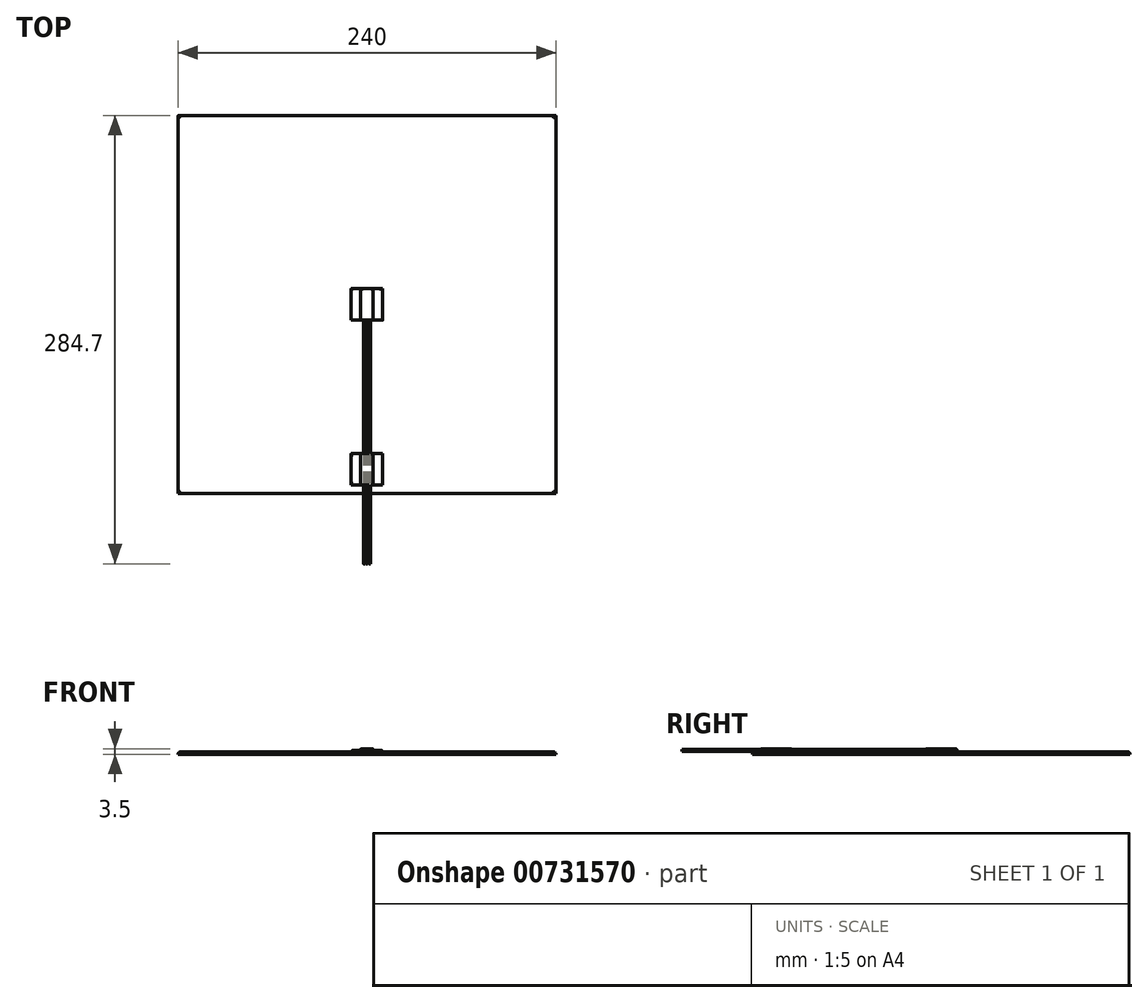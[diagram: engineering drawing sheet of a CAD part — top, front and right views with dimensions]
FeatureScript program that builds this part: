
annotation { "Feature Type Name" : "Feature", "Feature Type Description" : "" }
export const myFeature = defineFeature(function(context is Context, id is Id, definition is map)
    precondition{}
    {
        {
            var Q0;
            Q0=qCreatedBy(makeId("Top.planeOp"),FACE);
            var sketch = newSketch(context, id + "F0", { "sketchPlane" : qUnion([Q0])});
            skCircle(sketch, "E0.cCircle", {"center": v(0, 0) * mm, "radius": 120 * mm, "construction": true});
            skLineSegment(sketch, "E0.0", {"start": v(-120, 120) * mm, "end": v(120, 120) * mm});
            skLineSegment(sketch, "E0.1", {"start": v(120, 120) * mm, "end": v(120, -120) * mm});
            skLineSegment(sketch, "E0.2", {"start": v(120, -120) * mm, "end": v(-120, -120) * mm});
            skLineSegment(sketch, "E0.3", {"start": v(-120, -120) * mm, "end": v(-120, 120) * mm});
            skPoint(sketch, "E0.0.midPoint", {"position": v(0, 120) * mm});
            skSolve(sketch);
        }
        {
            var Q0;
            Q0 = qSketchRegion(id + "F0", true);
            extrude(context, id + "F1", {"entities" : qUnion([Q0]), "depth" : 1.5 * mm, "offsetDistance" : 25 * mm});
        }
        {
            var Q0;
            Q0=makeQuery(id+"F1.opExtrude","CAP_FACE",FACE,{"disambiguationData":[OSD([sQuery(id+"F0.wireOp",EDGE,"E0.0"),sQuery(id+"F0.wireOp",EDGE,"E0.1"),sQuery(id+"F0.wireOp",EDGE,"E0.2"),sQuery(id+"F0.wireOp",EDGE,"E0.3")])],"isStart":false});
            fillet(context, id + "F2", {"entities" : qUnion([Q0]), "radius" : 1.5 * mm, "tangentPropagation" : true, "allowEdgeOverflow" : false});
        }
        {
            var Q0;
            Q0=makeQuery(id+"F1.opExtrude","CAP_FACE",FACE,{"disambiguationData":[OSD([sQuery(id+"F0.wireOp",EDGE,"E0.0"),sQuery(id+"F0.wireOp",EDGE,"E0.1"),sQuery(id+"F0.wireOp",EDGE,"E0.2"),sQuery(id+"F0.wireOp",EDGE,"E0.3")])],"isStart":false});
            var sketch = newSketch(context, id + "F3", { "sketchPlane" : qUnion([Q0])});
            skCircle(sketch, "E1.cCircle", {"center": v(0, 0) * mm, "radius": 10 * mm, "construction": true});
            skLineSegment(sketch, "E1.0", {"start": v(-10, 10) * mm, "end": v(10, 10) * mm});
            skLineSegment(sketch, "E1.1", {"start": v(10, 10) * mm, "end": v(10, -10) * mm});
            skLineSegment(sketch, "E1.2", {"start": v(10, -10) * mm, "end": v(-10, -10) * mm});
            skLineSegment(sketch, "E1.3", {"start": v(-10, -10) * mm, "end": v(-10, 10) * mm});
            skPoint(sketch, "E1.0.midPoint", {"position": v(0, 10) * mm});
            skLineSegment(sketch, "E2", {"start": v(0, 0) * mm, "end": v(0, -105) * mm, "construction": true});
            skCircle(sketch, "E3.cCircle", {"center": v(0, -105) * mm, "radius": 10 * mm, "construction": true});
            skLineSegment(sketch, "E3.0", {"start": v(-10, -95) * mm, "end": v(10, -95) * mm});
            skLineSegment(sketch, "E3.1", {"start": v(10, -95) * mm, "end": v(10, -115) * mm});
            skLineSegment(sketch, "E3.2", {"start": v(10, -115) * mm, "end": v(-10, -115) * mm});
            skLineSegment(sketch, "E3.3", {"start": v(-10, -115) * mm, "end": v(-10, -95) * mm});
            skPoint(sketch, "E3.0.midPoint", {"position": v(0, -95) * mm});
            skSolve(sketch);
        }
        {
            var Q0;
            Q0=qCreatedBy(makeId("Front.planeOp"),FACE);
            var sketch = newSketch(context, id + "F4", { "sketchPlane" : qUnion([Q0])});
            skLineSegment(sketch, "E4", {"start": v(-10, 1.5) * mm, "end": v(-10, 2.5) * mm});
            skLineSegment(sketch, "E5", {"start": v(-10, 2.5) * mm, "end": v(-4, 2.5) * mm});
            skLineSegment(sketch, "E6", {"start": v(4, 2.5) * mm, "end": v(10, 2.5) * mm});
            skLineSegment(sketch, "E7", {"start": v(10, 2.5) * mm, "end": v(10, 1.5) * mm});
            skLineSegment(sketch, "E8", {"start": v(10, 1.5) * mm, "end": v(-10, 1.5) * mm});
            skLineSegment(sketch, "E9", {"start": v(-4, 2.5) * mm, "end": v(-4, 3.5) * mm});
            skLineSegment(sketch, "E10", {"start": v(-4, 3.5) * mm, "end": v(4, 3.5) * mm});
            skLineSegment(sketch, "E11", {"start": v(4, 3.5) * mm, "end": v(4, 2.5) * mm});
            skPoint(sketch, "E12.orphan", {"position": v(0, 2.5) * mm});
            skSolve(sketch);
        }
        {
            var Q0;
            Q0 = qSketchRegion(id + "F4", true);
            extrude(context, id + "F5", {"entities" : qUnion([Q0]), "depth" : 20 * mm, "offsetDistance" : 25 * mm, "symmetric" : true});
        }
        {
            var Q0;
            Q0=makeQuery(id+"F5.opExtrude","SWEPT_EDGE",EDGE,{"disambiguationData":[OSD([sQuery(id+"F4.wireOp",EDGE,"E10"),sQuery(id+"F4.wireOp",EDGE,"E11")])]});
            var Q1;
            Q1=makeQuery(id+"F5.opExtrude","SWEPT_EDGE",EDGE,{"disambiguationData":[OSD([sQuery(id+"F4.wireOp",EDGE,"E6"),sQuery(id+"F4.wireOp",EDGE,"E11")])]});
            var Q2;
            Q2=makeQuery(id+"F5.opExtrude","SWEPT_EDGE",EDGE,{"disambiguationData":[OSD([sQuery(id+"F4.wireOp",EDGE,"E9"),sQuery(id+"F4.wireOp",EDGE,"E10")])]});
            var Q3;
            Q3=makeQuery(id+"F5.opExtrude","SWEPT_EDGE",EDGE,{"disambiguationData":[OSD([sQuery(id+"F4.wireOp",EDGE,"E5"),sQuery(id+"F4.wireOp",EDGE,"E9")])]});
            fillet(context, id + "F6", {"entities" : qUnion([Q0, Q1, Q2, Q3]), "radius" : 0.5 * mm, "tangentPropagation" : true, "allowEdgeOverflow" : false});
        }
        {
            var Q0;
            Q0=makeQuery(id+"F5.opExtrude","SWEPT_EDGE",EDGE,{"disambiguationData":[OSD([sQuery(id+"F4.wireOp",EDGE,"E6"),sQuery(id+"F4.wireOp",EDGE,"E7")])]});
            var Q1;
            Q1=makeQuery(id+"F5.opExtrude","SWEPT_EDGE",EDGE,{"disambiguationData":[OSD([sQuery(id+"F4.wireOp",EDGE,"E4"),sQuery(id+"F4.wireOp",EDGE,"E5")])]});
            var Q2;
            Q2=makeQuery(id+"F5.opExtrude","CAP_EDGE",EDGE,{"disambiguationData":[OSD([sQuery(id+"F4.wireOp",EDGE,"E5")])],"isStart":true});
            var Q3;
            Q3=makeQuery(id+"F5.opExtrude","CAP_EDGE",EDGE,{"disambiguationData":[OSD([sQuery(id+"F4.wireOp",EDGE,"E5")])],"isStart":false});
            fillet(context, id + "F7", {"entities" : qUnion([Q0, Q1, Q2, Q3]), "radius" : 1 * mm, "tangentPropagation" : true, "allowEdgeOverflow" : false});
        }
        {
            var Q0;
            Q0=makeQuery(id+"F5.opExtrude","SWEPT_BODY",BODY,{"disambiguationData":[OSD([sQuery(id+"F4.wireOp",EDGE,"E4"),sQuery(id+"F4.wireOp",EDGE,"E5"),sQuery(id+"F4.wireOp",EDGE,"E6"),sQuery(id+"F4.wireOp",EDGE,"E7"),sQuery(id+"F4.wireOp",EDGE,"E8"),sQuery(id+"F4.wireOp",EDGE,"E9"),sQuery(id+"F4.wireOp",EDGE,"E10"),sQuery(id+"F4.wireOp",EDGE,"E11")])]});
            transform(context, id + "F8", {"entities" : qUnion([Q0]), "transformType" : TransformType.TRANSLATION_3D, "dx" : 0 * mm, "dy" : -104.7 * mm, "dz" : 0 * mm, "makeCopy" : true});
        }
        {
            var Q0;
            Q0=makeQuery(id+"F8.opPattern","COPY",FACE,{"derivedFrom":makeQuery(id+"F5.opExtrude","CAP_FACE",FACE,{"disambiguationData":[OSD([sQuery(id+"F4.wireOp",EDGE,"E4"),sQuery(id+"F4.wireOp",EDGE,"E5"),sQuery(id+"F4.wireOp",EDGE,"E6"),sQuery(id+"F4.wireOp",EDGE,"E7"),sQuery(id+"F4.wireOp",EDGE,"E8"),sQuery(id+"F4.wireOp",EDGE,"E9"),sQuery(id+"F4.wireOp",EDGE,"E10"),sQuery(id+"F4.wireOp",EDGE,"E11")])],"isStart":false}),"instanceName":"1"});
            var sketch = newSketch(context, id + "F9", { "sketchPlane" : qUnion([Q0])});
            skCircle(sketch, "E13", {"center": v(0, 2.5) * mm, "radius": 0.5 * mm});
            skLineSegment(sketch, "E14", {"start": v(0, 0) * mm, "end": v(0, 3.15) * mm, "construction": true});
            skLineSegment(sketch, "E15", {"start": v(-1.75, 2.5) * mm, "end": v(1.75, 2.5) * mm, "construction": true});
            skCircle(sketch, "E16", {"center": v(-1.75, 2.5) * mm, "radius": 0.5 * mm});
            skCircle(sketch, "E17", {"center": v(1.75, 2.5) * mm, "radius": 0.5 * mm});
            skSolve(sketch);
        }
        {
            var Q0;
            {var subQ0=sQuery(id+"F9.wireOp",EDGE,"E13");var subQ1=sQuery(id+"F4.wireOp",EDGE,"E10");var subQ2=makeQuery(id+"F8.opPattern","COPY",EDGE,{"derivedFrom":makeQuery(id+"F7.opFillet","BLEND_EDGE",EDGE,{"blendedFrom":[makeQuery(id+"F5.opExtrude","CAP_EDGE",EDGE,{"disambiguationData":[OSD([subQ1])],"isStart":false}),makeQuery(id+"F5.opExtrude","CAP_FACE",FACE,{"disambiguationData":[OSD([sQuery(id+"F4.wireOp",EDGE,"E4"),sQuery(id+"F4.wireOp",EDGE,"E5"),sQuery(id+"F4.wireOp",EDGE,"E6"),sQuery(id+"F4.wireOp",EDGE,"E7"),sQuery(id+"F4.wireOp",EDGE,"E8"),sQuery(id+"F4.wireOp",EDGE,"E9"),subQ1,sQuery(id+"F4.wireOp",EDGE,"E11")])],"isStart":false})],"blendedInto":[makeQuery(id+"F5.opExtrude","CAP_FACE",FACE,{"disambiguationData":[OSD([sQuery(id+"F4.wireOp",EDGE,"E4"),sQuery(id+"F4.wireOp",EDGE,"E5"),sQuery(id+"F4.wireOp",EDGE,"E6"),sQuery(id+"F4.wireOp",EDGE,"E7"),sQuery(id+"F4.wireOp",EDGE,"E8"),sQuery(id+"F4.wireOp",EDGE,"E9"),subQ1,sQuery(id+"F4.wireOp",EDGE,"E11")])],"isStart":false})]}),"instanceName":"1"});var subQ3=makeQuery(id+"F9.imprint","INTERSECT",VERTEX,{"disambiguationData":[OD(0.0)],"derivedFrom":[subQ2,subQ0]});Q0=makeQuery(id+"F9.imprint","IMPRINT",FACE,{"disambiguationData":[TD([[makeQuery(id+"F9.imprint","IMPRINT",EDGE,{"disambiguationData":[TD([[subQ3,1.0]])],"derivedFrom":subQ0}),1.0]])]});}
            var Q1;
            {var subQ0=sQuery(id+"F9.wireOp",EDGE,"E13");var subQ1=sQuery(id+"F4.wireOp",EDGE,"E10");var subQ2=makeQuery(id+"F8.opPattern","COPY",EDGE,{"derivedFrom":makeQuery(id+"F7.opFillet","BLEND_EDGE",EDGE,{"blendedFrom":[makeQuery(id+"F5.opExtrude","CAP_EDGE",EDGE,{"disambiguationData":[OSD([subQ1])],"isStart":false}),makeQuery(id+"F5.opExtrude","CAP_FACE",FACE,{"disambiguationData":[OSD([sQuery(id+"F4.wireOp",EDGE,"E4"),sQuery(id+"F4.wireOp",EDGE,"E5"),sQuery(id+"F4.wireOp",EDGE,"E6"),sQuery(id+"F4.wireOp",EDGE,"E7"),sQuery(id+"F4.wireOp",EDGE,"E8"),sQuery(id+"F4.wireOp",EDGE,"E9"),subQ1,sQuery(id+"F4.wireOp",EDGE,"E11")])],"isStart":false})],"blendedInto":[makeQuery(id+"F5.opExtrude","CAP_FACE",FACE,{"disambiguationData":[OSD([sQuery(id+"F4.wireOp",EDGE,"E4"),sQuery(id+"F4.wireOp",EDGE,"E5"),sQuery(id+"F4.wireOp",EDGE,"E6"),sQuery(id+"F4.wireOp",EDGE,"E7"),sQuery(id+"F4.wireOp",EDGE,"E8"),sQuery(id+"F4.wireOp",EDGE,"E9"),subQ1,sQuery(id+"F4.wireOp",EDGE,"E11")])],"isStart":false})]}),"instanceName":"1"});var subQ3=makeQuery(id+"F9.imprint","INTERSECT",VERTEX,{"disambiguationData":[OD(0.0)],"derivedFrom":[subQ2,subQ0]});Q1=makeQuery(id+"F9.imprint","IMPRINT",FACE,{"disambiguationData":[TD([[makeQuery(id+"F9.imprint","IMPRINT",EDGE,{"disambiguationData":[TD([[subQ3,-1.0]])],"derivedFrom":subQ0}),1.0]])]});}
            var Q2;
            {var subQ0=sQuery(id+"F9.wireOp",EDGE,"E17");var subQ1=sQuery(id+"F4.wireOp",EDGE,"E10");var subQ2=makeQuery(id+"F8.opPattern","COPY",EDGE,{"derivedFrom":makeQuery(id+"F7.opFillet","BLEND_EDGE",EDGE,{"blendedFrom":[makeQuery(id+"F5.opExtrude","CAP_EDGE",EDGE,{"disambiguationData":[OSD([subQ1])],"isStart":false}),makeQuery(id+"F5.opExtrude","CAP_FACE",FACE,{"disambiguationData":[OSD([sQuery(id+"F4.wireOp",EDGE,"E4"),sQuery(id+"F4.wireOp",EDGE,"E5"),sQuery(id+"F4.wireOp",EDGE,"E6"),sQuery(id+"F4.wireOp",EDGE,"E7"),sQuery(id+"F4.wireOp",EDGE,"E8"),sQuery(id+"F4.wireOp",EDGE,"E9"),subQ1,sQuery(id+"F4.wireOp",EDGE,"E11")])],"isStart":false})],"blendedInto":[makeQuery(id+"F5.opExtrude","CAP_FACE",FACE,{"disambiguationData":[OSD([sQuery(id+"F4.wireOp",EDGE,"E4"),sQuery(id+"F4.wireOp",EDGE,"E5"),sQuery(id+"F4.wireOp",EDGE,"E6"),sQuery(id+"F4.wireOp",EDGE,"E7"),sQuery(id+"F4.wireOp",EDGE,"E8"),sQuery(id+"F4.wireOp",EDGE,"E9"),subQ1,sQuery(id+"F4.wireOp",EDGE,"E11")])],"isStart":false})]}),"instanceName":"1"});var subQ3=makeQuery(id+"F9.imprint","INTERSECT",VERTEX,{"disambiguationData":[OD(0.0)],"derivedFrom":[subQ2,subQ0]});Q2=makeQuery(id+"F9.imprint","IMPRINT",FACE,{"disambiguationData":[TD([[makeQuery(id+"F9.imprint","IMPRINT",EDGE,{"disambiguationData":[TD([[subQ3,-1.0]])],"derivedFrom":subQ0}),1.0]])]});}
            var Q3;
            {var subQ0=sQuery(id+"F9.wireOp",EDGE,"E17");var subQ1=sQuery(id+"F4.wireOp",EDGE,"E10");var subQ2=makeQuery(id+"F8.opPattern","COPY",EDGE,{"derivedFrom":makeQuery(id+"F7.opFillet","BLEND_EDGE",EDGE,{"blendedFrom":[makeQuery(id+"F5.opExtrude","CAP_EDGE",EDGE,{"disambiguationData":[OSD([subQ1])],"isStart":false}),makeQuery(id+"F5.opExtrude","CAP_FACE",FACE,{"disambiguationData":[OSD([sQuery(id+"F4.wireOp",EDGE,"E4"),sQuery(id+"F4.wireOp",EDGE,"E5"),sQuery(id+"F4.wireOp",EDGE,"E6"),sQuery(id+"F4.wireOp",EDGE,"E7"),sQuery(id+"F4.wireOp",EDGE,"E8"),sQuery(id+"F4.wireOp",EDGE,"E9"),subQ1,sQuery(id+"F4.wireOp",EDGE,"E11")])],"isStart":false})],"blendedInto":[makeQuery(id+"F5.opExtrude","CAP_FACE",FACE,{"disambiguationData":[OSD([sQuery(id+"F4.wireOp",EDGE,"E4"),sQuery(id+"F4.wireOp",EDGE,"E5"),sQuery(id+"F4.wireOp",EDGE,"E6"),sQuery(id+"F4.wireOp",EDGE,"E7"),sQuery(id+"F4.wireOp",EDGE,"E8"),sQuery(id+"F4.wireOp",EDGE,"E9"),subQ1,sQuery(id+"F4.wireOp",EDGE,"E11")])],"isStart":false})]}),"instanceName":"1"});var subQ3=makeQuery(id+"F9.imprint","INTERSECT",VERTEX,{"disambiguationData":[OD(0.0)],"derivedFrom":[subQ2,subQ0]});Q3=makeQuery(id+"F9.imprint","IMPRINT",FACE,{"disambiguationData":[TD([[makeQuery(id+"F9.imprint","IMPRINT",EDGE,{"disambiguationData":[TD([[subQ3,1.0]])],"derivedFrom":subQ0}),1.0]])]});}
            var Q4;
            {var subQ0=sQuery(id+"F9.wireOp",EDGE,"E16");var subQ1=sQuery(id+"F4.wireOp",EDGE,"E10");var subQ2=makeQuery(id+"F8.opPattern","COPY",EDGE,{"derivedFrom":makeQuery(id+"F7.opFillet","BLEND_EDGE",EDGE,{"blendedFrom":[makeQuery(id+"F5.opExtrude","CAP_EDGE",EDGE,{"disambiguationData":[OSD([subQ1])],"isStart":false}),makeQuery(id+"F5.opExtrude","CAP_FACE",FACE,{"disambiguationData":[OSD([sQuery(id+"F4.wireOp",EDGE,"E4"),sQuery(id+"F4.wireOp",EDGE,"E5"),sQuery(id+"F4.wireOp",EDGE,"E6"),sQuery(id+"F4.wireOp",EDGE,"E7"),sQuery(id+"F4.wireOp",EDGE,"E8"),sQuery(id+"F4.wireOp",EDGE,"E9"),subQ1,sQuery(id+"F4.wireOp",EDGE,"E11")])],"isStart":false})],"blendedInto":[makeQuery(id+"F5.opExtrude","CAP_FACE",FACE,{"disambiguationData":[OSD([sQuery(id+"F4.wireOp",EDGE,"E4"),sQuery(id+"F4.wireOp",EDGE,"E5"),sQuery(id+"F4.wireOp",EDGE,"E6"),sQuery(id+"F4.wireOp",EDGE,"E7"),sQuery(id+"F4.wireOp",EDGE,"E8"),sQuery(id+"F4.wireOp",EDGE,"E9"),subQ1,sQuery(id+"F4.wireOp",EDGE,"E11")])],"isStart":false})]}),"instanceName":"1"});var subQ3=makeQuery(id+"F9.imprint","INTERSECT",VERTEX,{"disambiguationData":[OD(0.0)],"derivedFrom":[subQ2,subQ0]});Q4=makeQuery(id+"F9.imprint","IMPRINT",FACE,{"disambiguationData":[TD([[makeQuery(id+"F9.imprint","IMPRINT",EDGE,{"disambiguationData":[TD([[subQ3,1.0]])],"derivedFrom":subQ0}),1.0]])]});}
            var Q5;
            {var subQ0=sQuery(id+"F9.wireOp",EDGE,"E16");var subQ1=sQuery(id+"F4.wireOp",EDGE,"E10");var subQ2=makeQuery(id+"F8.opPattern","COPY",EDGE,{"derivedFrom":makeQuery(id+"F7.opFillet","BLEND_EDGE",EDGE,{"blendedFrom":[makeQuery(id+"F5.opExtrude","CAP_EDGE",EDGE,{"disambiguationData":[OSD([subQ1])],"isStart":false}),makeQuery(id+"F5.opExtrude","CAP_FACE",FACE,{"disambiguationData":[OSD([sQuery(id+"F4.wireOp",EDGE,"E4"),sQuery(id+"F4.wireOp",EDGE,"E5"),sQuery(id+"F4.wireOp",EDGE,"E6"),sQuery(id+"F4.wireOp",EDGE,"E7"),sQuery(id+"F4.wireOp",EDGE,"E8"),sQuery(id+"F4.wireOp",EDGE,"E9"),subQ1,sQuery(id+"F4.wireOp",EDGE,"E11")])],"isStart":false})],"blendedInto":[makeQuery(id+"F5.opExtrude","CAP_FACE",FACE,{"disambiguationData":[OSD([sQuery(id+"F4.wireOp",EDGE,"E4"),sQuery(id+"F4.wireOp",EDGE,"E5"),sQuery(id+"F4.wireOp",EDGE,"E6"),sQuery(id+"F4.wireOp",EDGE,"E7"),sQuery(id+"F4.wireOp",EDGE,"E8"),sQuery(id+"F4.wireOp",EDGE,"E9"),subQ1,sQuery(id+"F4.wireOp",EDGE,"E11")])],"isStart":false})]}),"instanceName":"1"});var subQ3=makeQuery(id+"F9.imprint","INTERSECT",VERTEX,{"disambiguationData":[OD(0.0)],"derivedFrom":[subQ2,subQ0]});Q5=makeQuery(id+"F9.imprint","IMPRINT",FACE,{"disambiguationData":[TD([[makeQuery(id+"F9.imprint","IMPRINT",EDGE,{"disambiguationData":[TD([[subQ3,-1.0]])],"derivedFrom":subQ0}),1.0]])]});}
            var Q6;
            Q6=makeQuery(id+"F5.opExtrude","CAP_FACE",FACE,{"disambiguationData":[OSD([sQuery(id+"F4.wireOp",EDGE,"E4"),sQuery(id+"F4.wireOp",EDGE,"E5"),sQuery(id+"F4.wireOp",EDGE,"E6"),sQuery(id+"F4.wireOp",EDGE,"E7"),sQuery(id+"F4.wireOp",EDGE,"E8"),sQuery(id+"F4.wireOp",EDGE,"E9"),sQuery(id+"F4.wireOp",EDGE,"E10"),sQuery(id+"F4.wireOp",EDGE,"E11")])],"isStart":false});
            extrude(context, id + "F10", {"entities" : qUnion([Q0, Q1, Q2, Q3, Q4, Q5]), "endBound" : BoundingType.UP_TO_SURFACE, "oppositeDirection" : true, "depth" : 25 * mm, "endBoundEntityFace" : qUnion([Q6]), "offsetDistance" : 25 * mm, "hasSecondDirection" : true, "secondDirectionOppositeDirection" : false, "secondDirectionDepth" : 50 * mm});
        }
    });
